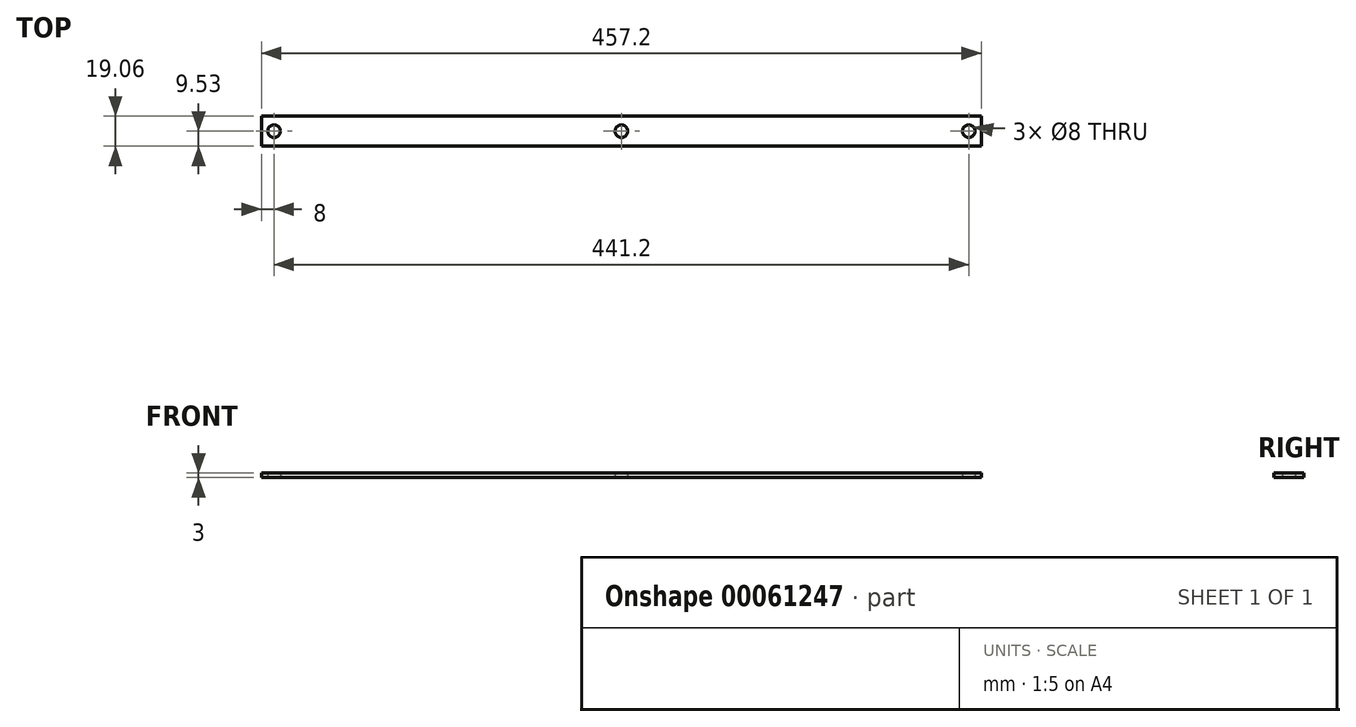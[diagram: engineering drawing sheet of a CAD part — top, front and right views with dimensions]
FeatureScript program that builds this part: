
annotation { "Feature Type Name" : "Feature", "Feature Type Description" : "" }
export const myFeature = defineFeature(function(context is Context, id is Id, definition is map)
    precondition{}
    {
        {
            var Q0;
            Q0=qCreatedBy(makeId("Top.planeOp"),FACE);
            var sketch = newSketch(context, id + "F0", { "sketchPlane" : qUnion([Q0])});
            skLineSegment(sketch, "E0.rect.bottom", {"start": v(-228.6, -9.53) * mm, "end": v(228.6, -9.53) * mm});
            skLineSegment(sketch, "E0.rect.top", {"start": v(-228.6, 9.53) * mm, "end": v(228.6, 9.53) * mm});
            skLineSegment(sketch, "E0.rect.left", {"start": v(-228.6, -9.53) * mm, "end": v(-228.6, 9.53) * mm});
            skLineSegment(sketch, "E0.rect.right", {"start": v(228.6, -9.53) * mm, "end": v(228.6, 9.53) * mm});
            skPoint(sketch, "E0.rect.middle", {"position": v(0, 0) * mm});
            skCircle(sketch, "E1", {"center": v(-220.6, 0) * mm, "radius": 4 * mm});
            skCircle(sketch, "E2.MirrorC", {"center": v(220.6, 0) * mm, "radius": 4 * mm});
            skCircle(sketch, "E3", {"center": v(0, 0) * mm, "radius": 4 * mm});
            skSolve(sketch);
        }
        {
            var Q0;
            Q0=makeQuery(id+"F0.imprint","IMPRINT",FACE,{"disambiguationData":[TD([[makeQuery(id+"F0.imprint","IMPRINT",EDGE,{"derivedFrom":sQuery(id+"F0.wireOp",EDGE,"E0.rect.bottom")}),1.0]])]});
            extrude(context, id + "F1", {"entities" : qUnion([Q0]), "depth" : 3 * mm});
        }
    });
